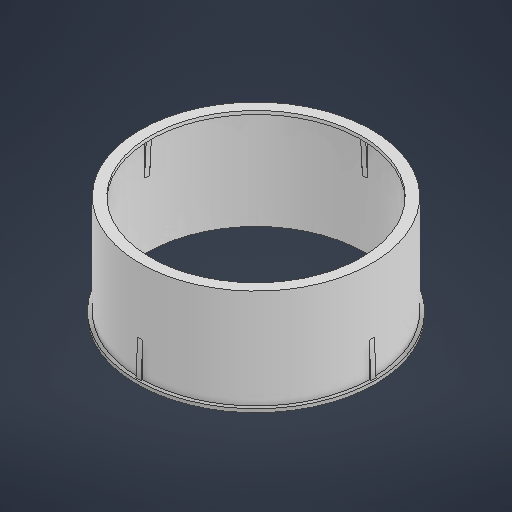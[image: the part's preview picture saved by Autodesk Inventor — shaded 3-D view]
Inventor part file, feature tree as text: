
AUTODESK INVENTOR PART (.ipt)
format: ipt  version: 2025 (Build 290162000, 162)  size: 550,400 bytes
history: native  units: in
note: dims shown in document units (in); Inventor stores cm internally (conversion verified against a paired STEP export)
features: rib x44, sketch x28, other x12, extrude x5, plane x1
ambient origin geometry x8: Origin, YZ Plane, XZ Plane, XY Plane, X Axis, Y Axis, Z Axis, Center Point
bodies: Solid1 (feature_tree)
feature tree (90):
  other  "Table"
  other  "C .Replace - 01"
  other  "C .Replace - 02"
  other  "C .Replace - 03"
  other  "C .Replace - 04"
  other  "C .Replace - 05"
  other  "C .Replace - 06"
  other  "C .Replace - 07"
  other  "C .Replace - 08"
  other  "C .Replace - 09"
  other  "C .Replace - 10"
  other  "C .Replace - Face"
  sketch  "Sketch1"  dims[d5=0.0in d7=0.0in]
  extrude  "Extrusion1"  TaperAngle=0.0deg  [1 undecoded]
  extrude  "Extrusion2"  Depth=10.0394in
  sketch  "Sketch2"  dims[d28=0.1969in d29=3.937in d31=360.0deg]
  extrude  "Extrusion7"  Depth=3.937in TaperAngle=360.0deg
  plane  "Work Plane2"
  extrude  "Extrusion8"  Depth=0.3937in
  extrude  "Extrusion30"  Depth=0.2165in
  sketch  "Sketch26"  dims[d236=0.3937in d237=0.0in]
  sketch  "Sketch27"  dims[d552=0.7874in]
  sketch  "Sketch28"  dims[d553=0.7874in]
  sketch  "Sketch29"  dims[d554=0.0394in d555=0.0394in d556=0.0in d557=0.0in d558=0.0394in d559=0.0394in]
  sketch  "Sketch30"  dims[d560=0.0394in d561=0.0394in d562=0.0in d563=0.0in d564=0.0394in d565=0.0394in]
  sketch  "Sketch32"  dims[d567=0.7874in]
  sketch  "Sketch33"  dims[d568=0.0394in d569=0.0394in d570=0.0in d571=0.0in d572=0.0394in d573=0.0394in]
  sketch  "Sketch34"  dims[d574=0.0394in]
  sketch  "Sketch35"  dims[d575=0.1181in d576=0.0in d577=0.0in d578=0.0394in d579=0.0394in]
  sketch  "Sketch36"  dims[d580=0.7874in]
  sketch  "Sketch37"  dims[d581=0.7874in]
  sketch  "Sketch38"  dims[d582=0.0394in]
  sketch  "Sketch39"  dims[d583=0.1181in d584=0.0in d585=0.0in d586=0.0394in d587=0.0394in]
  sketch  "Sketch40"  dims[d588=0.0394in]
  sketch  "Sketch41"  dims[d589=0.1181in d590=0.0in d591=0.0in d592=0.0394in d593=0.0394in]
  sketch  "Sketch42"  dims[d594=0.7874in]
  sketch  "Sketch43"  dims[d595=0.7874in]
  sketch  "Sketch44"  dims[d596=0.0394in]
  sketch  "Sketch45"  dims[d597=0.1181in d598=0.0in d599=0.0in d600=0.0394in d601=0.0394in]
  sketch  "Sketch46"  dims[d602=0.0394in]
  sketch  "Sketch47"  dims[d603=0.1181in d604=0.0in d605=0.0in d606=0.0394in d607=0.0394in d608=0.7874in d609=0.7874in d610=0.0394in d611=0.1181in d612=0.0in d613=0.0in d614=0.0394in d615=0.0394in d616=0.0394in d617=0.1181in d618=0.0in d619=0.0in d620=0.0394in d621=0.0394in d623=0.7874in d636=0.7874in d637=0.7874in d638=0.0394in d639=0.1181in d640=0.0in d641=0.0in d642=0.0394in d643=0.0394in d644=0.0394in d645=0.1181in d646=0.0in d647=0.0in d648=0.0394in d649=0.0394in d650=0.7874in d651=0.7874in d652=0.0394in d653=0.1181in d654=0.0in d655=0.0in d656=0.0394in d657=0.0394in d658=0.0394in d659=0.1181in d660=0.0in d661=0.0in d662=0.0394in d663=0.0394in d664=0.7874in d665=0.7874in d666=0.0394in d667=0.1181in d668=0.0in d669=0.0in d670=0.0394in d671=0.0394in d672=0.0394in d673=0.1181in d674=0.0in d675=0.0in d676=0.0394in d677=0.0394in d678=0.7874in d679=0.7874in d680=0.0394in d681=0.1181in d682=0.0in d683=0.0in d684=0.0394in d685=0.0394in d686=0.0394in d687=0.1181in d688=0.0in d689=0.0in d690=0.0394in d691=0.0394in d692=0.7874in d693=0.7874in d694=0.0394in d695=0.1181in d696=0.0in d697=0.0in d698=0.0394in d699=0.0394in d700=0.0394in d701=0.1181in d702=0.0in d703=0.0in d704=0.0394in d705=0.0394in d706=0.7874in d720=0.7874in d721=0.7874in d722=0.0394in d723=0.1181in d724=0.0in d725=0.0in d726=0.0394in d727=0.0394in d728=0.0394in d729=0.1181in d730=0.0in d731=0.0in d732=0.0394in d733=0.0394in d734=0.7874in d735=0.7874in d736=0.0394in d737=0.1181in d738=0.0in d739=0.0in d740=0.0394in d741=0.0394in d742=0.0394in d743=0.1181in d744=0.0in d745=0.0in d746=0.0394in d747=0.0394in d748=0.7874in d749=0.7874in d750=0.0394in d751=0.1181in d752=0.0in d753=0.0in d754=0.0394in d755=0.0394in d756=0.0394in d757=0.1181in d758=0.0in d759=0.0in d760=0.0394in d761=0.0394in d762=0.7874in d763=0.7874in d764=0.0394in d765=0.1181in d766=0.0in d767=0.0in d768=0.0394in d769=0.0394in d770=0.0394in d771=0.1181in d772=0.0in d773=0.0in d774=0.0394in d775=0.0394in d776=0.7874in d777=0.7874in d778=0.0394in d779=0.1181in d780=0.0in d781=0.0in d782=0.0394in d783=0.0394in d784=0.0394in d785=0.1181in d786=0.0in d787=0.0in d788=0.0394in d789=0.0394in d790=0.7874in d791=0.7874in d792=0.0394in d793=0.1181in d794=0.0in d795=0.0in d796=0.0394in d797=0.0394in d798=0.0394in d799=0.1181in d800=0.0in d801=0.0in d802=0.0394in d803=0.0394in d804=0.7874in d805=0.7874in d806=0.0394in d807=0.1181in d808=0.0in d809=0.0in d810=0.0394in d811=0.0394in d812=0.0394in d813=0.1181in d814=0.0in d815=0.0in d816=0.0394in d817=0.0394in d818=0.7874in d819=0.7874in d820=0.0394in d821=0.1181in d822=0.0in d823=0.0in d824=0.0394in d825=0.0394in d826=0.0394in d827=0.1181in d828=0.0in d829=0.0in d830=0.0394in d831=0.0394in d832=0.7874in d833=0.0394in d834=0.1181in d835=0.0in d836=0.0in d837=0.0394in d838=0.0394in d839=0.0394in d840=0.1181in d841=0.0in d842=0.0in d843=0.0394in d844=0.0394in d845=0.7874in d846=0.0394in d847=0.1181in d848=0.0in d849=0.0in d850=0.0394in d851=0.0394in d852=0.0394in d853=0.1181in d854=0.0in d855=0.0in d856=0.0394in d857=0.0394in d858=0.7874in d859=0.0394in d860=0.0394in d861=0.0in d862=0.0in d863=0.0394in d864=0.0394in d865=0.0394in d866=0.0394in d867=0.0in d868=0.0in d869=0.0394in d870=0.0394in d871=0.7874in d872=0.0394in d873=0.1181in d874=0.0in d875=0.0in d876=0.0394in d877=0.0394in d878=0.0394in d879=0.1181in d880=0.0in d881=0.0in d882=0.0394in d883=0.0394in d113=0.0197in d114=0.0344in d115=0.0197in d116=0.0344in d167=0.0197in d168=0.0344in d169=0.0197in d170=0.0344in d215=0.0197in d216=0.0344in d217=0.0197in d218=0.0344in d219=0.0in d220=0.0in]
  rib  "Rib46"
  rib  "Rib47"
  sketch  "Sketch31"  dims[d566=0.7874in]
  rib  "Rib48"
  rib  "Rib49"
  rib  "Rib50"
  rib  "Rib51"
  rib  "Rib52"
  rib  "Rib53"
  rib  "Rib92"
  rib  "Rib93"
  rib  "Rib54"
  rib  "Rib55"
  rib  "Rib58"
  rib  "Rib59"
  rib  "Rib60"
  rib  "Rib61"
  rib  "Rib62"
  rib  "Rib63"
  rib  "Rib64"
  rib  "Rib65"
  rib  "Rib66"
  rib  "Rib67"
  rib  "Rib70"
  rib  "Rib71"
  rib  "Rib72"
  rib  "Rib73"
  rib  "Rib74"
  rib  "Rib75"
  rib  "Rib76"
  rib  "Rib77"
  rib  "Rib78"
  rib  "Rib79"
  rib  "Rib80"
  rib  "Rib81"
  rib  "Rib82"
  rib  "Rib83"
  rib  "Rib84"
  rib  "Rib85"
  rib  "Rib86"
  rib  "Rib87"
  rib  "Rib88"
  rib  "Rib89"
  rib  "Rib90"
  rib  "Rib91"
  sketch  "Sketch3"  dims[d33=0.3937in d34=0.0in d52=4.5276in]
  sketch  "Sketch Circular Pattern1"  dims[d18=0.0in d27=10.0394in]
  sketch  "Sketch24"  dims[d232=2.3622in d234=360.0deg]
  sketch  "Sketch Circular Pattern4"  dims[d230=4.0157in d231=0.2165in]
note: 1 required parameter value undecoded (feature->parameter linkage not recoverable at this tier; creation-order binding heuristic only, values carry confidence <= 0.55)
